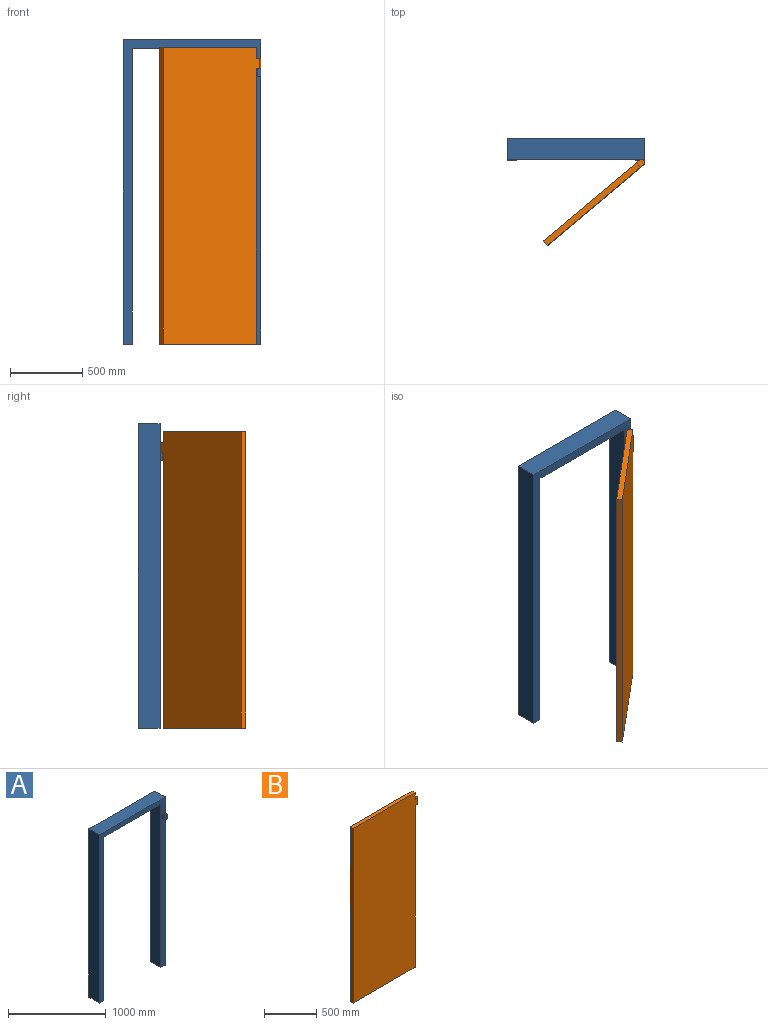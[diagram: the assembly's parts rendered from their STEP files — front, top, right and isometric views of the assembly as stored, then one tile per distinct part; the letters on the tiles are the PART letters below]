
ASSEMBLY  parts=2 mates=1
PART A: 18 faces, bbox 950x190x2100 mm
  f0: plane 2100x950mm, normal (0,-1,0), area 309500mm2, adj f1,f2,f3,f4,f5,f7,f8,f9
  f1: plane 150x62.5mm, normal (0,0,-1), area 9375mm2, adj f0,f5,f6,f9
  f2: plane 150x62.5mm, normal (0,0,-1), area 9375mm2, adj f0,f3,f6,f7
  f3: plane 2100x170mm, normal (1,0,0), area 316000mm2, adj f0,f2,f4,f6,f10,f12,f17
  f4: plane 950x150mm, normal (0,0,1), area 142500mm2, adj f0,f3,f5,f6
  f5: plane 2100x150mm, normal (-1,0,0), area 315000mm2, adj f0,f1,f4,f6
  f6: plane 2100x950mm, normal (0,1,0), area 312000mm2, adj f1,f2,f3,f4,f5,f7,f8,f9
  f7: plane 2040x150mm, normal (-1,0,0), area 306000mm2, adj f0,f2,f6,f8
  f8: plane 825x150mm, normal (0,0,-1), area 123750mm2, adj f0,f6,f7,f9
  f9: plane 2040x150mm, normal (1,0,0), area 306000mm2, adj f0,f1,f6,f8
  f10: plane 50x40mm, normal (0,0,1), area 1514.2mm2, adj f0,f3,f11,f13,f14,f16,f17
  f11: plane 50x20mm, normal (-1,0,0), area 1000mm2, adj f0,f10,f12,f16
  f12: plane 50x40mm, normal (0,0,-1), area 1828.3mm2, adj f0,f3,f11,f13,f16,f17
  f13: plane 50x10mm, normal (0,-1,0), area 500mm2, adj f10,f12,f16,f17
  f14: cylinder r=10mm len=25mm, axis (0,0,-1), area 1570.8mm2, adj f10,f15
  f15: plane 20x20mm, normal (0,0,1), area 314.2mm2, adj f14
  f16: cylinder r=20mm len=50mm, axis (0,0,1), area 1570.8mm2, adj f10,f11,f12,f13
  f17: cylinder r=20mm len=50mm, axis (0,0,-1), area 1570.8mm2, adj f3,f10,f12,f13
PART B: 12 faces, bbox 890x40x2050 mm
  f0: plane 1900x40mm, normal (1,0,0), area 76000mm2, adj f2,f5,f6,f7
  f1: plane 2050x40mm, normal (-1,0,0), area 82000mm2, adj f2,f4,f5,f6
  f2: plane 840x40mm, normal (0,0,-1), area 33600mm2, adj f0,f1,f5,f6
  f3: plane 80x40mm, normal (1,0,0), area 3200mm2, adj f4,f5,f6,f8
  f4: plane 840x40mm, normal (0,0,1), area 33600mm2, adj f1,f3,f5,f6
  f5: plane 2050x870mm, normal (0,-1,0), area 1724100mm2, adj f0,f1,f2,f3,f4,f7,f8,f11
  f6: plane 2050x870mm, normal (0,1,0), area 1724100mm2, adj f0,f1,f2,f3,f4,f7,f8,f11
  f7: plane 50x40mm, normal (0,0,-1), area 1514.2mm2, adj f0,f5,f6,f9,f11
  f8: plane 50x40mm, normal (0,0,1), area 1828.3mm2, adj f3,f5,f6,f11
  f9: cylinder r=10mm len=25mm, axis (0,0,-1), area 1570.8mm2, adj f7,f10
  f10: plane 20x20mm, normal (0,0,-1), area 314.2mm2, adj f9
  f11: cylinder r=20mm len=70mm, axis (0,0,-1), area 4398.2mm2, adj f5,f6,f7,f8
PLACE A t=(-32.49,125.53,73.94)mm fixed
PLACE B rot(axis=(0,0,1),40deg) t=(-36.49,-203.49,73.94)mm
MATE revolute A.f14 <-> B.f9  axis (0,0,1) through (417.51,-44.47,948.94)mm
